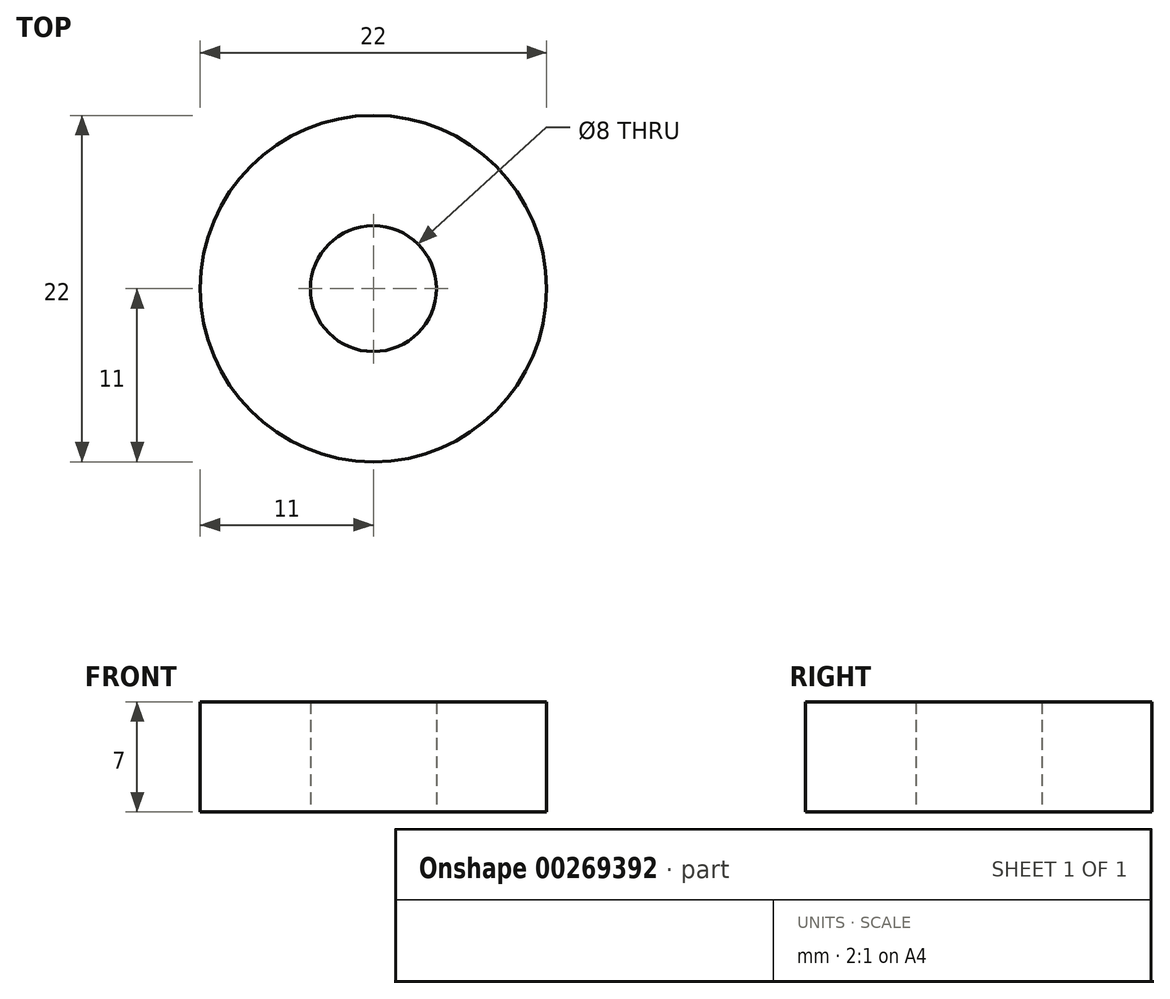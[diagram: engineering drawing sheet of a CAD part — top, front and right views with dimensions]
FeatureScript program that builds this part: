
annotation { "Feature Type Name" : "Feature", "Feature Type Description" : "" }
export const myFeature = defineFeature(function(context is Context, id is Id, definition is map)
    precondition{}
    {
        {
            var Q0;
            Q0=qCreatedBy(makeId("Top.planeOp"),FACE);
            var sketch = newSketch(context, id + "F0", { "sketchPlane" : qUnion([Q0])});
            skCircle(sketch, "E0", {"center": v(0, 0) * mm, "radius": 11 * mm});
            skCircle(sketch, "E1", {"center": v(0, 0) * mm, "radius": 4 * mm});
            skSolve(sketch);
        }
        {
            var Q0;
            Q0 = qSketchRegion(id + "F0", true);
            extrude(context, id + "F1", {"entities" : qUnion([Q0]), "endBound" : BoundingType.SYMMETRIC, "depth" : 7 * mm});
        }
    });
